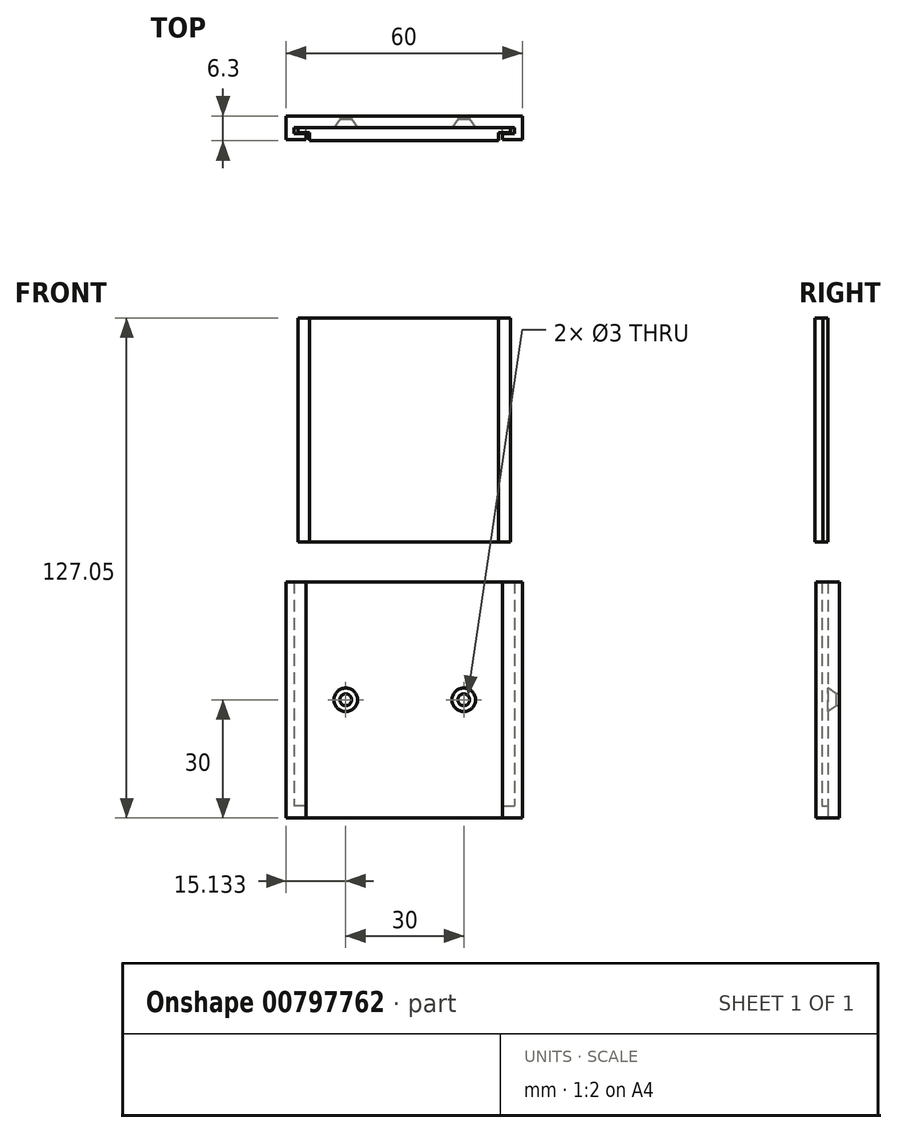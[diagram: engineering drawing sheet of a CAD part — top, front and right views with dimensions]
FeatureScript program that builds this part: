
annotation { "Feature Type Name" : "Feature", "Feature Type Description" : "" }
export const myFeature = defineFeature(function(context is Context, id is Id, definition is map)
    precondition{}
    {
        {
            var Q0;
            Q0=qCreatedBy(makeId("Front.planeOp"),FACE);
            var sketch = newSketch(context, id + "F0", { "sketchPlane" : qUnion([Q0])});
            skLineSegment(sketch, "E0.bottom", {"start": v(-30, 30) * mm, "end": v(30, 30) * mm});
            skLineSegment(sketch, "E0.top", {"start": v(-30, -30) * mm, "end": v(30, -30) * mm});
            skLineSegment(sketch, "E0.left", {"start": v(-30, 30) * mm, "end": v(-30, -30) * mm});
            skLineSegment(sketch, "E0.right", {"start": v(30, 30) * mm, "end": v(30, -30) * mm});
            skSolve(sketch);
        }
        {
            var Q0;
            Q0 = qSketchRegion(id + "F0", true);
            extrude(context, id + "F1", {"entities" : qUnion([Q0]), "depth" : 3 * mm, "offsetDistance" : 25 * mm});
        }
        {
            var Q0;
            Q0=makeQuery(id+"F1.opExtrude","CAP_FACE",FACE,{"disambiguationData":[OSD([sQuery(id+"F0.wireOp",EDGE,"E0.bottom"),sQuery(id+"F0.wireOp",EDGE,"E0.top"),sQuery(id+"F0.wireOp",EDGE,"E0.left"),sQuery(id+"F0.wireOp",EDGE,"E0.right")])],"isStart":false});
            var sketch = newSketch(context, id + "F2", { "sketchPlane" : qUnion([Q0])});
            skLineSegment(sketch, "E1.bottom", {"start": v(28, 30) * mm, "end": v(30, 30) * mm});
            skLineSegment(sketch, "E1.top", {"start": v(28, -30) * mm, "end": v(30, -30) * mm});
            skLineSegment(sketch, "E1.left", {"start": v(28, 30) * mm, "end": v(28, -30) * mm});
            skLineSegment(sketch, "E1.right", {"start": v(30, 30) * mm, "end": v(30, -30) * mm});
            skLineSegment(sketch, "E2.bottom", {"start": v(-30, 30) * mm, "end": v(-28, 30) * mm});
            skLineSegment(sketch, "E2.top", {"start": v(-30, -30) * mm, "end": v(-28, -30) * mm});
            skLineSegment(sketch, "E2.left", {"start": v(-30, 30) * mm, "end": v(-30, -30) * mm});
            skLineSegment(sketch, "E2.right", {"start": v(-28, 30) * mm, "end": v(-28, -30) * mm});
            skSolve(sketch);
        }
        {
            var Q0;
            Q0 = qSketchRegion(id + "F2", true);
            extrude(context, id + "F3", {"entities" : qUnion([Q0]), "operationType" : NewBodyOperationType.ADD, "depth" : 3 * mm, "offsetDistance" : 25 * mm});
        }
        {
            var Q0;
            {var subQ0=sQuery(id+"F0.wireOp",EDGE,"E0.top");var subQ1=sQuery(id+"F0.wireOp",EDGE,"E0.bottom");Q0=makeQuery(id+"F3.boolean.opBoolean","SPLIT",FACE,{"disambiguationData":[TD([makeQuery(id+"F3.opExtrude","SWEPT_FACE",FACE,{"disambiguationData":[OSD([sQuery(id+"F2.wireOp",EDGE,"E1.left")])]})])],"derivedFrom":makeQuery(id+"F1.opExtrude","CAP_FACE",FACE,{"disambiguationData":[OSD([subQ1,subQ0,sQuery(id+"F0.wireOp",EDGE,"E0.left"),sQuery(id+"F0.wireOp",EDGE,"E0.right")])],"isStart":false})});}
            var sketch = newSketch(context, id + "F4", { "sketchPlane" : qUnion([Q0])});
            skPoint(sketch, "E3", {"position": v(15.13, 0) * mm});
            skPoint(sketch, "E4", {"position": v(-14.87, 0) * mm});
            skSolve(sketch);
        }
        {
            var Q0;
            Q0=sQuery(id+"F4.wireOp",VERTEX,"ef8c367e-c422-41f7-a125-bbbf9948105a");
            var Q1;
            Q1=sQuery(id+"F4.wireOp",VERTEX,"43de9364-d0b8-4cde-9da4-838a787500fd");
            var Q2;
            Q2=sQuery(id+"F4.wireOp",VERTEX,"E3");
            var Q3;
            Q3=sQuery(id+"F4.wireOp",VERTEX,"E4");
            var Q4;
            Q4=makeQuery(id+"F1.opExtrude","SWEPT_BODY",BODY,{"disambiguationData":[OSD([sQuery(id+"F0.wireOp",EDGE,"E0.bottom"),sQuery(id+"F0.wireOp",EDGE,"E0.top"),sQuery(id+"F0.wireOp",EDGE,"E0.left"),sQuery(id+"F0.wireOp",EDGE,"E0.right")])]});
            hole(context, id + "F5", {"style" : HoleStyle.C_SINK, "endStyle" : HoleEndStyle.THROUGH, "holeDiameter" : 3 * mm, "cSinkDiameter" : 6 * mm, "cSinkAngle" : 70 * degree, "majorDiameter" : 5 * mm, "isTappedThrough" : true, "tappedDepth" : 12 * mm, "tapClearance" : 3, "locations" : qUnion([Q0, Q1, Q2, Q3]), "scope" : qUnion([Q4])});
        }
        {
            var Q0;
            Q0=makeQuery(id+"F3.opExtrude","SWEPT_FACE",FACE,{"disambiguationData":[OSD([sQuery(id+"F2.wireOp",EDGE,"E1.left")])]});
            var sketch = newSketch(context, id + "F6", { "sketchPlane" : qUnion([Q0])});
            skLineSegment(sketch, "E5.bottom", {"start": v(6, 30) * mm, "end": v(4.5, 30) * mm});
            skLineSegment(sketch, "E5.top", {"start": v(6, -30) * mm, "end": v(4.5, -30) * mm});
            skLineSegment(sketch, "E5.left", {"start": v(6, 30) * mm, "end": v(6, -30) * mm});
            skLineSegment(sketch, "E5.right", {"start": v(4.5, 30) * mm, "end": v(4.5, -30) * mm});
            skLineSegment(sketch, "E6.bottom", {"start": v(4.5, -30) * mm, "end": v(3, -30) * mm});
            skLineSegment(sketch, "E6.top", {"start": v(4.5, -27) * mm, "end": v(3, -27) * mm});
            skLineSegment(sketch, "E6.left", {"start": v(4.5, -30) * mm, "end": v(4.5, -27) * mm});
            skLineSegment(sketch, "E6.right", {"start": v(3, -30) * mm, "end": v(3, -27) * mm});
            skSolve(sketch);
        }
        {
            var Q0;
            Q0 = qSketchRegion(id + "F6", true);
            extrude(context, id + "F7", {"entities" : qUnion([Q0]), "operationType" : NewBodyOperationType.ADD, "depth" : 3 * mm, "offsetDistance" : 25 * mm});
        }
        {
            var Q0;
            Q0=makeQuery(id+"F3.opExtrude","SWEPT_FACE",FACE,{"disambiguationData":[OSD([sQuery(id+"F2.wireOp",EDGE,"E2.right")])]});
            var sketch = newSketch(context, id + "F8", { "sketchPlane" : qUnion([Q0])});
            skLineSegment(sketch, "E7.bottom", {"start": v(-6, 30) * mm, "end": v(-4.5, 30) * mm});
            skLineSegment(sketch, "E7.top", {"start": v(-6, -30) * mm, "end": v(-4.5, -30) * mm});
            skLineSegment(sketch, "E7.left", {"start": v(-6, 30) * mm, "end": v(-6, -30) * mm});
            skLineSegment(sketch, "E7.right", {"start": v(-4.5, 30) * mm, "end": v(-4.5, -30) * mm});
            skLineSegment(sketch, "E8.bottom", {"start": v(-4.5, -30) * mm, "end": v(-3, -30) * mm});
            skLineSegment(sketch, "E8.top", {"start": v(-4.5, -27) * mm, "end": v(-3, -27) * mm});
            skLineSegment(sketch, "E8.left", {"start": v(-4.5, -30) * mm, "end": v(-4.5, -27) * mm});
            skLineSegment(sketch, "E8.right", {"start": v(-3, -30) * mm, "end": v(-3, -27) * mm});
            skSolve(sketch);
        }
        {
            var Q0;
            Q0 = qSketchRegion(id + "F8", true);
            extrude(context, id + "F9", {"entities" : qUnion([Q0]), "operationType" : NewBodyOperationType.ADD, "depth" : 3 * mm, "offsetDistance" : 25 * mm});
        }
        {
            var Q0;
            Q0=makeQuery(id+"F1.opExtrude","CAP_FACE",FACE,{"disambiguationData":[OSD([sQuery(id+"F0.wireOp",EDGE,"E0.bottom"),sQuery(id+"F0.wireOp",EDGE,"E0.top"),sQuery(id+"F0.wireOp",EDGE,"E0.left"),sQuery(id+"F0.wireOp",EDGE,"E0.right")])],"isStart":false});
            var sketch = newSketch(context, id + "F10", { "sketchPlane" : qUnion([Q0])});
            skLineSegment(sketch, "E9.bottom", {"start": v(-27, 97.05) * mm, "end": v(27, 97.05) * mm});
            skLineSegment(sketch, "E9.top", {"start": v(-27, 40.05) * mm, "end": v(27, 40.05) * mm});
            skLineSegment(sketch, "E9.left", {"start": v(-27, 97.05) * mm, "end": v(-27, 40.05) * mm});
            skLineSegment(sketch, "E9.right", {"start": v(27, 97.05) * mm, "end": v(27, 40.05) * mm});
            skSolve(sketch);
        }
        {
            var Q0;
            Q0 = qSketchRegion(id + "F10", true);
            extrude(context, id + "F11", {"entities" : qUnion([Q0]), "depth" : 1.2 * mm, "offsetDistance" : 25 * mm});
        }
        {
            var Q0;
            Q0=makeQuery(id+"F11.opExtrude","CAP_FACE",FACE,{"disambiguationData":[OSD([sQuery(id+"F10.wireOp",EDGE,"E9.bottom"),sQuery(id+"F10.wireOp",EDGE,"E9.top"),sQuery(id+"F10.wireOp",EDGE,"E9.left"),sQuery(id+"F10.wireOp",EDGE,"E9.right")])],"isStart":false});
            var sketch = newSketch(context, id + "F12", { "sketchPlane" : qUnion([Q0])});
            skLineSegment(sketch, "E10.bottom", {"start": v(24, 97.05) * mm, "end": v(-24, 97.05) * mm});
            skLineSegment(sketch, "E10.top", {"start": v(24, 40.05) * mm, "end": v(-24, 40.05) * mm});
            skLineSegment(sketch, "E10.left", {"start": v(24, 97.05) * mm, "end": v(24, 40.05) * mm});
            skLineSegment(sketch, "E10.right", {"start": v(-24, 97.05) * mm, "end": v(-24, 40.05) * mm});
            skSolve(sketch);
        }
        {
            var Q0;
            Q0 = qSketchRegion(id + "F12", true);
            extrude(context, id + "F13", {"entities" : qUnion([Q0]), "operationType" : NewBodyOperationType.ADD, "depth" : 2.1 * mm, "offsetDistance" : 25 * mm});
        }
    });
